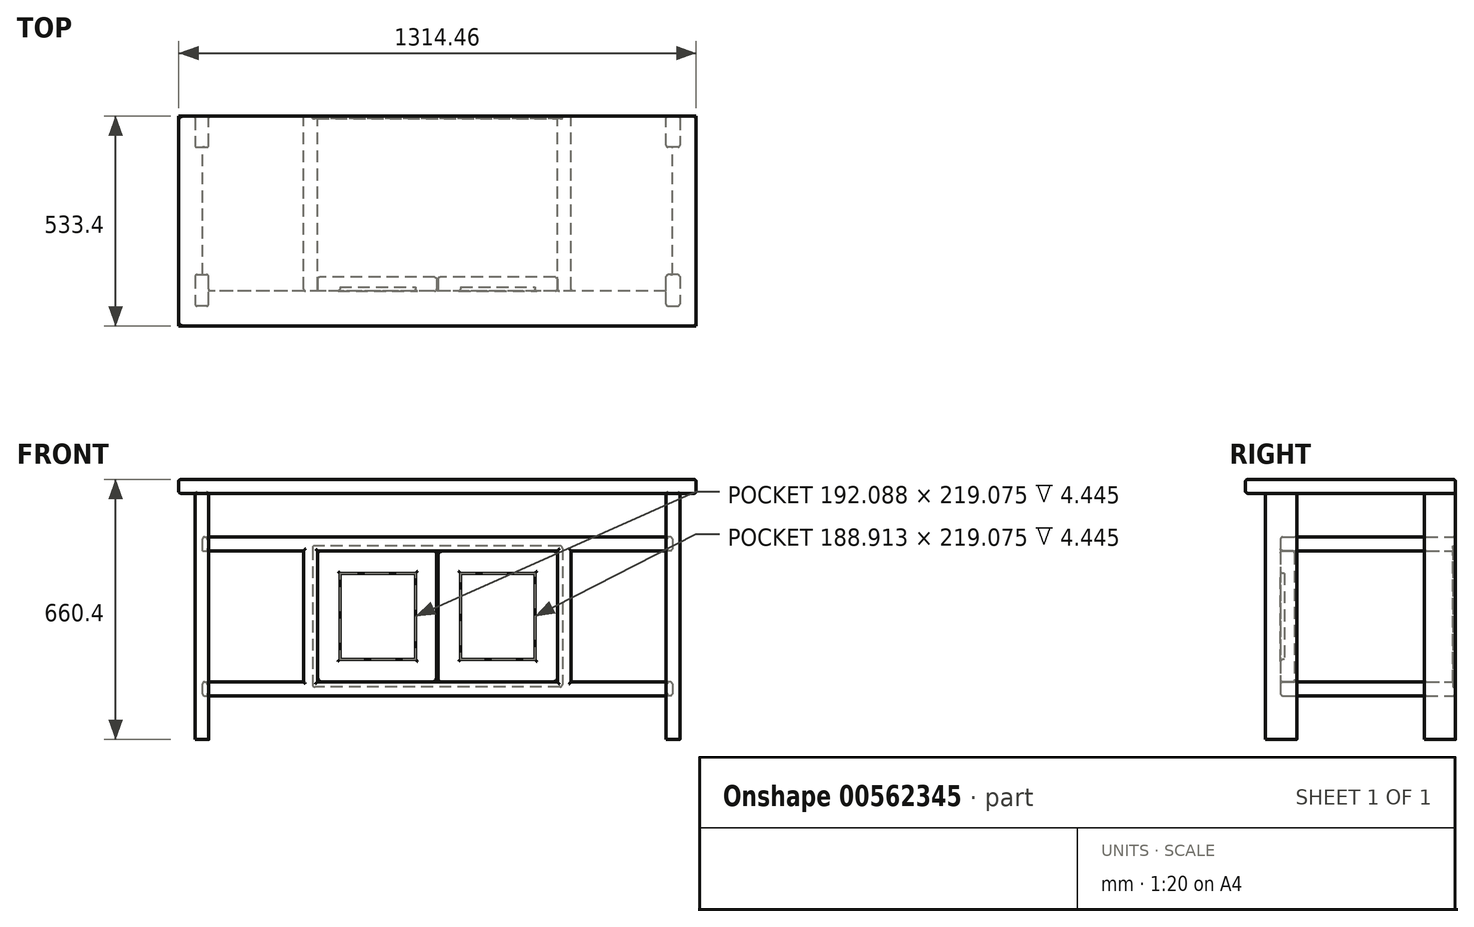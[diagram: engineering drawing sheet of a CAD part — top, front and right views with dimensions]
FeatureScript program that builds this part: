
annotation { "Feature Type Name" : "Feature", "Feature Type Description" : "" }
export const myFeature = defineFeature(function(context is Context, id is Id, definition is map)
    precondition{}
    {
        {
            var Q0;
            Q0=qCreatedBy(makeId("Front.planeOp"),FACE);
            var sketch = newSketch(context, id + "F0", { "sketchPlane" : qUnion([Q0])});
            skLineSegment(sketch, "E0.bottom", {"start": v(657.23, 660.4) * mm, "end": v(-657.23, 660.4) * mm});
            skLineSegment(sketch, "E0.top", {"start": v(657.22, 625.48) * mm, "end": v(-657.23, 625.48) * mm});
            skLineSegment(sketch, "E0.left", {"start": v(657.23, 660.4) * mm, "end": v(657.23, 625.48) * mm});
            skLineSegment(sketch, "E0.right", {"start": v(-657.23, 660.4) * mm, "end": v(-657.23, 625.48) * mm});
            skPoint(sketch, "E0.middle", {"position": v(0, 642.94) * mm});
            skLineSegment(sketch, "E1.bottom", {"start": v(596.9, 514.35) * mm, "end": v(-596.9, 514.35) * mm});
            skLineSegment(sketch, "E1.top", {"start": v(596.9, 479.43) * mm, "end": v(339.73, 479.43) * mm});
            skLineSegment(sketch, "E1.left", {"start": v(596.9, 514.35) * mm, "end": v(596.9, 479.43) * mm});
            skLineSegment(sketch, "E1.right", {"start": v(-596.9, 514.35) * mm, "end": v(-596.9, 479.43) * mm});
            skPoint(sketch, "E1.middle", {"position": v(0, 496.89) * mm});
            skLineSegment(sketch, "E2.bottom", {"start": v(596.9, 146.05) * mm, "end": v(339.73, 146.05) * mm});
            skLineSegment(sketch, "E2.top", {"start": v(596.9, 111.13) * mm, "end": v(-596.9, 111.13) * mm});
            skLineSegment(sketch, "E2.left", {"start": v(596.9, 146.05) * mm, "end": v(596.9, 111.13) * mm});
            skLineSegment(sketch, "E2.right", {"start": v(-596.9, 146.05) * mm, "end": v(-596.9, 111.13) * mm});
            skPoint(sketch, "E2.middle", {"position": v(0, 128.59) * mm});
            skLineSegment(sketch, "E3", {"start": v(304.8, 479.43) * mm, "end": v(304.8, 146.05) * mm});
            skLineSegment(sketch, "E4", {"start": v(339.73, 479.43) * mm, "end": v(339.73, 146.05) * mm});
            skLineSegment(sketch, "E5", {"start": v(0, 0) * mm, "end": v(0, -92.6) * mm, "construction": true});
            skLineSegment(sketch, "E6.MirrorCS", {"start": v(-304.8, 479.43) * mm, "end": v(-304.8, 146.05) * mm});
            skLineSegment(sketch, "E7.MirrorCS", {"start": v(-339.73, 479.43) * mm, "end": v(-339.73, 146.05) * mm});
            skLineSegment(sketch, "E8.trimOffspring", {"start": v(304.8, 479.43) * mm, "end": v(-304.8, 479.43) * mm});
            skLineSegment(sketch, "E9.trimOffspring", {"start": v(304.8, 146.05) * mm, "end": v(-304.8, 146.05) * mm});
            skLineSegment(sketch, "E10.trimOffspring", {"start": v(-339.73, 146.05) * mm, "end": v(-596.9, 146.05) * mm});
            skLineSegment(sketch, "E11.trimOffspring", {"start": v(-339.73, 479.43) * mm, "end": v(-596.9, 479.43) * mm});
            skLineSegment(sketch, "E12", {"start": v(304.8, 479.43) * mm, "end": v(339.73, 479.43) * mm, "construction": true});
            skSolve(sketch);
        }
        {
            var Q0;
            Q0=makeQuery(id+"F0.imprint","IMPRINT",FACE,{"disambiguationData":[TD([[makeQuery(id+"F0.imprint","IMPRINT",EDGE,{"derivedFrom":sQuery(id+"F0.wireOp",EDGE,"E1.bottom")}),1.0]])]});
            extrude(context, id + "F1", {"entities" : qUnion([Q0]), "depth" : 444.5 * mm, "offsetDistance" : 25.4 * mm});
        }
        {
            var Q0;
            Q0=makeQuery(id+"F0.imprint","IMPRINT",FACE,{"disambiguationData":[TD([[makeQuery(id+"F0.imprint","IMPRINT",EDGE,{"derivedFrom":sQuery(id+"F0.wireOp",EDGE,"E0.bottom")}),1.0]])]});
            extrude(context, id + "F2", {"entities" : qUnion([Q0]), "depth" : 533.4 * mm, "offsetDistance" : 25.4 * mm});
        }
        {
            var Q0;
            Q0=qCreatedBy(makeId("Top.planeOp"),FACE);
            var sketch = newSketch(context, id + "F3", { "sketchPlane" : qUnion([Q0])});
            skLineSegment(sketch, "E13.bottom", {"start": v(-615.95, -79.37) * mm, "end": v(-581.03, -79.37) * mm});
            skLineSegment(sketch, "E13.top", {"start": v(-615.95, 0) * mm, "end": v(-581.03, 0) * mm});
            skLineSegment(sketch, "E13.left", {"start": v(-615.95, -79.38) * mm, "end": v(-615.95, 0) * mm});
            skLineSegment(sketch, "E13.right", {"start": v(-581.03, -79.38) * mm, "end": v(-581.03, 0) * mm});
            skLineSegment(sketch, "E14.bottom", {"start": v(-615.95, -482.6) * mm, "end": v(-581.03, -482.6) * mm});
            skLineSegment(sketch, "E14.top", {"start": v(-615.95, -403.23) * mm, "end": v(-581.03, -403.23) * mm});
            skLineSegment(sketch, "E14.left", {"start": v(-615.95, -482.6) * mm, "end": v(-615.95, -403.23) * mm});
            skLineSegment(sketch, "E14.right", {"start": v(-581.03, -482.6) * mm, "end": v(-581.03, -403.23) * mm});
            skLineSegment(sketch, "E15", {"start": v(0, 0) * mm, "end": v(0, -190.92) * mm, "construction": true});
            skLineSegment(sketch, "E16.MirrorCS", {"start": v(615.95, -79.37) * mm, "end": v(581.03, -79.37) * mm});
            skLineSegment(sketch, "E17.MirrorCS", {"start": v(615.95, 0) * mm, "end": v(581.03, 0) * mm});
            skLineSegment(sketch, "E18.MirrorCS", {"start": v(615.95, -482.6) * mm, "end": v(581.03, -482.6) * mm});
            skLineSegment(sketch, "E19.MirrorCS", {"start": v(615.95, -403.23) * mm, "end": v(581.03, -403.23) * mm});
            skLineSegment(sketch, "E20.MirrorCS", {"start": v(581.03, -482.6) * mm, "end": v(581.03, -403.23) * mm});
            skLineSegment(sketch, "E21.MirrorCS", {"start": v(615.95, -79.38) * mm, "end": v(615.95, 0) * mm});
            skLineSegment(sketch, "E22.MirrorCS", {"start": v(615.95, -482.6) * mm, "end": v(615.95, -403.23) * mm});
            skLineSegment(sketch, "E23.MirrorCS", {"start": v(581.03, -79.38) * mm, "end": v(581.03, 0) * mm});
            skSolve(sketch);
        }
        {
            var Q0;
            Q0 = qSketchRegion(id + "F3", true);
            var Q1;
            Q1=makeQuery(id+"F2.opExtrude","SWEPT_FACE",FACE,{"disambiguationData":[OSD([sQuery(id+"F0.wireOp",EDGE,"E0.top")])]});
            extrude(context, id + "F4", {"entities" : qUnion([Q0]), "operationType" : NewBodyOperationType.ADD, "endBound" : BoundingType.UP_TO_SURFACE, "depth" : 25.4 * mm, "endBoundEntityFace" : qUnion([Q1]), "offsetDistance" : 25.4 * mm});
        }
        {
            var Q0;
            Q0=makeQuery(id+"F4.boolean.opBoolean","MERGE",FACE,{"derivedFrom":[makeQuery(id+"F1.opExtrude","CAP_FACE",FACE,{"disambiguationData":[OSD([sQuery(id+"F0.wireOp",EDGE,"E1.bottom"),sQuery(id+"F0.wireOp",EDGE,"E1.top"),sQuery(id+"F0.wireOp",EDGE,"E1.left"),sQuery(id+"F0.wireOp",EDGE,"E1.right"),sQuery(id+"F0.wireOp",EDGE,"E2.bottom"),sQuery(id+"F0.wireOp",EDGE,"E2.top"),sQuery(id+"F0.wireOp",EDGE,"E2.left"),sQuery(id+"F0.wireOp",EDGE,"E2.right"),sQuery(id+"F0.wireOp",EDGE,"E3"),sQuery(id+"F0.wireOp",EDGE,"E4"),sQuery(id+"F0.wireOp",EDGE,"E6.MirrorCS"),sQuery(id+"F0.wireOp",EDGE,"E7.MirrorCS"),sQuery(id+"F0.wireOp",EDGE,"E8.trimOffspring"),sQuery(id+"F0.wireOp",EDGE,"E9.trimOffspring"),sQuery(id+"F0.wireOp",EDGE,"E10.trimOffspring"),sQuery(id+"F0.wireOp",EDGE,"E11.trimOffspring")])],"isStart":true}),makeQuery(id+"F2.opExtrude","CAP_FACE",FACE,{"disambiguationData":[OSD([sQuery(id+"F0.wireOp",EDGE,"E0.bottom"),sQuery(id+"F0.wireOp",EDGE,"E0.top"),sQuery(id+"F0.wireOp",EDGE,"E0.left"),sQuery(id+"F0.wireOp",EDGE,"E0.right")])],"isStart":true}),makeQuery(id+"F4.opExtrude","SWEPT_FACE",FACE,{"disambiguationData":[OSD([sQuery(id+"F3.wireOp",EDGE,"E13.top")])]}),makeQuery(id+"F4.opExtrude","SWEPT_FACE",FACE,{"disambiguationData":[OSD([sQuery(id+"F3.wireOp",EDGE,"E17.MirrorCS")])]})]});
            var sketch = newSketch(context, id + "F5", { "sketchPlane" : qUnion([Q0])});
            skLineSegment(sketch, "E24.0", {"start": v(-311.15, 492.13) * mm, "end": v(311.15, 492.13) * mm});
            skLineSegment(sketch, "E24.1", {"start": v(-317.5, 485.78) * mm, "end": v(-317.5, 139.7) * mm});
            skLineSegment(sketch, "E24.2", {"start": v(-311.15, 133.35) * mm, "end": v(311.15, 133.35) * mm});
            skLineSegment(sketch, "E24.3", {"start": v(317.5, 485.78) * mm, "end": v(317.5, 139.7) * mm});
            skPoint(sketch, "E25.visualSharp", {"position": v(-317.5, 492.13) * mm});
            skArc(sketch, "E25.filletArc", {"start": v(-311.15, 492.13) * mm, "mid": v(-315.64, 490.27) * mm, "end": v(-317.5, 485.78) * mm});
            skPoint(sketch, "E26.visualSharp", {"position": v(317.5, 492.13) * mm});
            skArc(sketch, "E26.filletArc", {"start": v(317.5, 485.78) * mm, "mid": v(315.64, 490.27) * mm, "end": v(311.15, 492.13) * mm});
            skPoint(sketch, "E27.visualSharp", {"position": v(317.5, 133.35) * mm});
            skArc(sketch, "E27.filletArc", {"start": v(311.15, 133.35) * mm, "mid": v(315.64, 135.2) * mm, "end": v(317.5, 139.7) * mm});
            skPoint(sketch, "E28.visualSharp", {"position": v(-317.5, 133.35) * mm});
            skArc(sketch, "E28.filletArc", {"start": v(-317.5, 139.7) * mm, "mid": v(-315.64, 135.2) * mm, "end": v(-311.15, 133.35) * mm});
            skSolve(sketch);
        }
        {
            var Q0;
            Q0 = qSketchRegion(id + "F5", true);
            extrude(context, id + "F6", {"entities" : qUnion([Q0]), "oppositeDirection" : true, "depth" : 6.35 * mm, "offsetDistance" : 25.4 * mm});
        }
        {
            var Q0;
            Q0=makeQuery(id+"F6.opExtrude","SWEPT_BODY",BODY,{"disambiguationData":[OSD([sQuery(id+"F5.wireOp",EDGE,"E24.0"),sQuery(id+"F5.wireOp",EDGE,"E24.1"),sQuery(id+"F5.wireOp",EDGE,"E24.2"),sQuery(id+"F5.wireOp",EDGE,"E24.3"),sQuery(id+"F5.wireOp",EDGE,"E25.filletArc"),sQuery(id+"F5.wireOp",EDGE,"E26.filletArc"),sQuery(id+"F5.wireOp",EDGE,"E27.filletArc"),sQuery(id+"F5.wireOp",EDGE,"E28.filletArc")])]});
            var Q1;
            Q1=makeQuery(id+"F1.opExtrude","SWEPT_BODY",BODY,{"disambiguationData":[OSD([sQuery(id+"F0.wireOp",EDGE,"E1.bottom"),sQuery(id+"F0.wireOp",EDGE,"E1.top"),sQuery(id+"F0.wireOp",EDGE,"E1.left"),sQuery(id+"F0.wireOp",EDGE,"E1.right"),sQuery(id+"F0.wireOp",EDGE,"E2.bottom"),sQuery(id+"F0.wireOp",EDGE,"E2.top"),sQuery(id+"F0.wireOp",EDGE,"E2.left"),sQuery(id+"F0.wireOp",EDGE,"E2.right"),sQuery(id+"F0.wireOp",EDGE,"E3"),sQuery(id+"F0.wireOp",EDGE,"E4"),sQuery(id+"F0.wireOp",EDGE,"E6.MirrorCS"),sQuery(id+"F0.wireOp",EDGE,"E7.MirrorCS"),sQuery(id+"F0.wireOp",EDGE,"E8.trimOffspring"),sQuery(id+"F0.wireOp",EDGE,"E9.trimOffspring"),sQuery(id+"F0.wireOp",EDGE,"E10.trimOffspring"),sQuery(id+"F0.wireOp",EDGE,"E11.trimOffspring")])]});
            booleanBodies(context, id + "F7", {"operationType" : BooleanOperationType.SUBTRACTION, "tools" : qUnion([Q0]), "targets" : qUnion([Q1]), "keepTools" : true});
        }
        {
            var Q0;
            Q0=makeQuery(id+"F1.opExtrude","CAP_FACE",FACE,{"disambiguationData":[OSD([sQuery(id+"F0.wireOp",EDGE,"E1.bottom"),sQuery(id+"F0.wireOp",EDGE,"E1.top"),sQuery(id+"F0.wireOp",EDGE,"E1.left"),sQuery(id+"F0.wireOp",EDGE,"E1.right"),sQuery(id+"F0.wireOp",EDGE,"E2.bottom"),sQuery(id+"F0.wireOp",EDGE,"E2.top"),sQuery(id+"F0.wireOp",EDGE,"E2.left"),sQuery(id+"F0.wireOp",EDGE,"E2.right"),sQuery(id+"F0.wireOp",EDGE,"E3"),sQuery(id+"F0.wireOp",EDGE,"E4"),sQuery(id+"F0.wireOp",EDGE,"E6.MirrorCS"),sQuery(id+"F0.wireOp",EDGE,"E7.MirrorCS"),sQuery(id+"F0.wireOp",EDGE,"E8.trimOffspring"),sQuery(id+"F0.wireOp",EDGE,"E9.trimOffspring"),sQuery(id+"F0.wireOp",EDGE,"E10.trimOffspring"),sQuery(id+"F0.wireOp",EDGE,"E11.trimOffspring")])],"isStart":false});
            var sketch = newSketch(context, id + "F8", { "sketchPlane" : qUnion([Q0])});
            skLineSegment(sketch, "E29.bottom", {"start": v(-304.8, 479.43) * mm, "end": v(-1.59, 479.43) * mm});
            skLineSegment(sketch, "E29.top", {"start": v(-304.8, 146.05) * mm, "end": v(-1.59, 146.05) * mm});
            skLineSegment(sketch, "E29.left", {"start": v(-304.8, 479.43) * mm, "end": v(-304.8, 146.05) * mm});
            skLineSegment(sketch, "E29.right", {"start": v(-1.59, 479.43) * mm, "end": v(-1.59, 146.05) * mm});
            skLineSegment(sketch, "E30.bottom", {"start": v(1.59, 146.05) * mm, "end": v(304.8, 146.05) * mm});
            skLineSegment(sketch, "E30.top", {"start": v(1.59, 479.43) * mm, "end": v(304.8, 479.43) * mm});
            skLineSegment(sketch, "E30.left", {"start": v(1.59, 146.05) * mm, "end": v(1.59, 479.43) * mm});
            skLineSegment(sketch, "E30.right", {"start": v(304.8, 146.05) * mm, "end": v(304.8, 479.43) * mm});
            skLineSegment(sketch, "E31.0", {"start": v(-247.65, 422.28) * mm, "end": v(-55.56, 422.28) * mm});
            skLineSegment(sketch, "E31.1", {"start": v(-247.65, 422.28) * mm, "end": v(-247.65, 203.2) * mm});
            skLineSegment(sketch, "E31.2", {"start": v(-247.65, 203.2) * mm, "end": v(-55.56, 203.2) * mm});
            skLineSegment(sketch, "E31.3", {"start": v(-55.56, 203.2) * mm, "end": v(-55.56, 422.28) * mm});
            skLineSegment(sketch, "E32.0", {"start": v(58.74, 422.28) * mm, "end": v(247.65, 422.28) * mm});
            skLineSegment(sketch, "E32.1", {"start": v(58.74, 203.2) * mm, "end": v(58.74, 422.28) * mm});
            skLineSegment(sketch, "E32.2", {"start": v(58.74, 203.2) * mm, "end": v(247.65, 203.2) * mm});
            skLineSegment(sketch, "E32.3", {"start": v(247.65, 203.2) * mm, "end": v(247.65, 422.28) * mm});
            skPoint(sketch, "E33", {"position": v(0, 111.13) * mm});
            skSolve(sketch);
        }
        {
            var Q0;
            Q0 = qSketchRegion(id + "F8", true);
            var Q1;
            Q1=makeQuery(id+"F8.imprint","IMPRINT",FACE,{"disambiguationData":[TD([[makeQuery(id+"F8.imprint","IMPRINT",EDGE,{"derivedFrom":sQuery(id+"F8.wireOp",EDGE,"E31.0")}),-1.0]])]});
            var Q2;
            Q2=makeQuery(id+"F8.imprint","IMPRINT",FACE,{"disambiguationData":[TD([[makeQuery(id+"F8.imprint","IMPRINT",EDGE,{"derivedFrom":sQuery(id+"F8.wireOp",EDGE,"E32.0")}),-1.0]])]});
            extrude(context, id + "F9", {"entities" : qUnion([Q0, Q1, Q2]), "oppositeDirection" : true, "depth" : 34.92 * mm, "offsetDistance" : 25.4 * mm});
        }
        {
            var Q0;
            Q0=makeQuery(id+"F8.imprint","IMPRINT",FACE,{"disambiguationData":[TD([[makeQuery(id+"F8.imprint","IMPRINT",EDGE,{"derivedFrom":sQuery(id+"F8.wireOp",EDGE,"E31.0")}),-1.0]])]});
            var Q1;
            Q1=makeQuery(id+"F8.imprint","IMPRINT",FACE,{"disambiguationData":[TD([[makeQuery(id+"F8.imprint","IMPRINT",EDGE,{"derivedFrom":sQuery(id+"F8.wireOp",EDGE,"E32.0")}),-1.0]])]});
            extrude(context, id + "F10", {"entities" : qUnion([Q0, Q1]), "operationType" : NewBodyOperationType.REMOVE, "oppositeDirection" : true, "depth" : 9.52 * mm, "offsetDistance" : 25.4 * mm});
        }
        {
            var Q0;
            Q0=makeQuery(id+"F2.opExtrude","SWEPT_FACE",FACE,{"disambiguationData":[OSD([sQuery(id+"F0.wireOp",EDGE,"E0.bottom")])]});
            var Q1;
            Q1=makeQuery(id+"F2.opExtrude","CAP_EDGE",EDGE,{"disambiguationData":[OSD([sQuery(id+"F0.wireOp",EDGE,"E0.top")])],"isStart":false});
            var Q2;
            Q2=makeQuery(id+"F2.opExtrude","SWEPT_EDGE",EDGE,{"disambiguationData":[OSD([sQuery(id+"F0.wireOp",EDGE,"E0.top"),sQuery(id+"F0.wireOp",EDGE,"E0.right")])]});
            var Q3;
            Q3=makeQuery(id+"F2.opExtrude","SWEPT_EDGE",EDGE,{"disambiguationData":[OSD([sQuery(id+"F0.wireOp",EDGE,"E0.top"),sQuery(id+"F0.wireOp",EDGE,"E0.left")])]});
            var Q4;
            Q4=makeQuery(id+"F1.opExtrude","CAP_EDGE",EDGE,{"disambiguationData":[OSD([sQuery(id+"F0.wireOp",EDGE,"E1.bottom")])],"isStart":false});
            var Q5;
            Q5=makeQuery(id+"F1.opExtrude","CAP_EDGE",EDGE,{"disambiguationData":[OSD([sQuery(id+"F0.wireOp",EDGE,"E1.top")])],"isStart":false});
            var Q6;
            Q6=makeQuery(id+"F1.opExtrude","SWEPT_EDGE",EDGE,{"disambiguationData":[OSD([sQuery(id+"F0.wireOp",EDGE,"E1.bottom"),sQuery(id+"F0.wireOp",EDGE,"E1.left")])]});
            var Q7;
            Q7=makeQuery(id+"F1.opExtrude","SWEPT_EDGE",EDGE,{"disambiguationData":[OSD([sQuery(id+"F0.wireOp",EDGE,"E1.top"),sQuery(id+"F0.wireOp",EDGE,"E1.left")])]});
            var Q8;
            Q8=makeQuery(id+"F1.opExtrude","CAP_EDGE",EDGE,{"disambiguationData":[OSD([sQuery(id+"F0.wireOp",EDGE,"E1.bottom")])],"isStart":true});
            var Q9;
            Q9=makeQuery(id+"F1.opExtrude","CAP_EDGE",EDGE,{"disambiguationData":[OSD([sQuery(id+"F0.wireOp",EDGE,"E1.top")])],"isStart":true});
            var Q10;
            Q10=makeQuery(id+"F1.opExtrude","CAP_EDGE",EDGE,{"disambiguationData":[OSD([sQuery(id+"F0.wireOp",EDGE,"E11.trimOffspring")])],"isStart":true});
            var Q11;
            Q11=makeQuery(id+"F1.opExtrude","SWEPT_EDGE",EDGE,{"disambiguationData":[OSD([sQuery(id+"F0.wireOp",EDGE,"E1.bottom"),sQuery(id+"F0.wireOp",EDGE,"E1.right")])]});
            var Q12;
            Q12=makeQuery(id+"F4.opExtrude","SWEPT_EDGE",EDGE,{"disambiguationData":[OSD([sQuery(id+"F3.wireOp",EDGE,"E13.bottom"),sQuery(id+"F3.wireOp",EDGE,"E13.left")])]});
            var Q13;
            Q13=makeQuery(id+"F4.opExtrude","SWEPT_EDGE",EDGE,{"disambiguationData":[OSD([sQuery(id+"F3.wireOp",EDGE,"E13.top"),sQuery(id+"F3.wireOp",EDGE,"E13.left")])]});
            var Q14;
            Q14=makeQuery(id+"F4.opExtrude","SWEPT_EDGE",EDGE,{"disambiguationData":[OSD([sQuery(id+"F3.wireOp",EDGE,"E14.top"),sQuery(id+"F3.wireOp",EDGE,"E14.left")])]});
            var Q15;
            Q15=makeQuery(id+"F4.opExtrude","SWEPT_EDGE",EDGE,{"disambiguationData":[OSD([sQuery(id+"F3.wireOp",EDGE,"E14.bottom"),sQuery(id+"F3.wireOp",EDGE,"E14.right")])]});
            var Q16;
            Q16=makeQuery(id+"F4.opExtrude","SWEPT_EDGE",EDGE,{"disambiguationData":[OSD([sQuery(id+"F3.wireOp",EDGE,"E14.bottom"),sQuery(id+"F3.wireOp",EDGE,"E14.left")])]});
            var Q17;
            Q17=makeQuery(id+"F4.opExtrude","SWEPT_EDGE",EDGE,{"disambiguationData":[OSD([sQuery(id+"F3.wireOp",EDGE,"E18.MirrorCS"),sQuery(id+"F3.wireOp",EDGE,"E20.MirrorCS")])]});
            var Q18;
            Q18=makeQuery(id+"F4.opExtrude","SWEPT_EDGE",EDGE,{"disambiguationData":[OSD([sQuery(id+"F3.wireOp",EDGE,"E18.MirrorCS"),sQuery(id+"F3.wireOp",EDGE,"E22.MirrorCS")])]});
            var Q19;
            Q19=makeQuery(id+"F4.opExtrude","SWEPT_EDGE",EDGE,{"disambiguationData":[OSD([sQuery(id+"F3.wireOp",EDGE,"E19.MirrorCS"),sQuery(id+"F3.wireOp",EDGE,"E22.MirrorCS")])]});
            var Q20;
            Q20=makeQuery(id+"F4.opExtrude","SWEPT_EDGE",EDGE,{"disambiguationData":[OSD([sQuery(id+"F3.wireOp",EDGE,"E16.MirrorCS"),sQuery(id+"F3.wireOp",EDGE,"E21.MirrorCS")])]});
            var Q21;
            Q21=makeQuery(id+"F4.opExtrude","SWEPT_EDGE",EDGE,{"disambiguationData":[OSD([sQuery(id+"F3.wireOp",EDGE,"E17.MirrorCS"),sQuery(id+"F3.wireOp",EDGE,"E21.MirrorCS")])]});
            var Q22;
            {var subQ0=sQuery(id+"F0.wireOp",EDGE,"E1.top");var subQ2=sQuery(id+"F3.wireOp",EDGE,"E17.MirrorCS");var subQ3=sQuery(id+"F3.wireOp",EDGE,"E23.MirrorCS");Q22=makeQuery(id+"F4.boolean.opBoolean","SPLIT",EDGE,{"disambiguationData":[TD([makeQuery(id+"F1.opExtrude","SWEPT_FACE",FACE,{"disambiguationData":[OSD([subQ0])]})])],"derivedFrom":makeQuery(id+"F4.opExtrude","SWEPT_EDGE",EDGE,{"disambiguationData":[OSD([subQ2,subQ3])]})});}
            var Q23;
            Q23=makeQuery(id+"F1.opExtrude","CAP_EDGE",EDGE,{"disambiguationData":[OSD([sQuery(id+"F0.wireOp",EDGE,"E2.bottom")])],"isStart":true});
            var Q24;
            Q24=makeQuery(id+"F1.opExtrude","CAP_EDGE",EDGE,{"disambiguationData":[OSD([sQuery(id+"F0.wireOp",EDGE,"E2.top")])],"isStart":true});
            var Q25;
            Q25=makeQuery(id+"F1.opExtrude","CAP_EDGE",EDGE,{"disambiguationData":[OSD([sQuery(id+"F0.wireOp",EDGE,"E4")])],"isStart":true});
            var Q26;
            {var subQ0=sQuery(id+"F3.wireOp",EDGE,"E16.MirrorCS");var subQ1=sQuery(id+"F3.wireOp",EDGE,"E23.MirrorCS");Q26=makeQuery(id+"F4.boolean.opBoolean","SPLIT",EDGE,{"disambiguationData":[TD([makeQuery(id+"F1.opExtrude","SWEPT_FACE",FACE,{"disambiguationData":[OSD([sQuery(id+"F0.wireOp",EDGE,"E1.bottom")])]})])],"derivedFrom":makeQuery(id+"F4.opExtrude","SWEPT_EDGE",EDGE,{"disambiguationData":[OSD([subQ0,subQ1])]})});}
            var Q27;
            {var subQ0=sQuery(id+"F3.wireOp",EDGE,"E23.MirrorCS");var subQ1=sQuery(id+"F3.wireOp",EDGE,"E16.MirrorCS");Q27=makeQuery(id+"F4.boolean.opBoolean","SPLIT",EDGE,{"disambiguationData":[TD([makeQuery(id+"F1.opExtrude","SWEPT_FACE",FACE,{"disambiguationData":[OSD([sQuery(id+"F0.wireOp",EDGE,"E1.top")])]})])],"derivedFrom":makeQuery(id+"F4.opExtrude","SWEPT_EDGE",EDGE,{"disambiguationData":[OSD([subQ1,subQ0])]})});}
            var Q28;
            {var subQ0=sQuery(id+"F3.wireOp",EDGE,"E16.MirrorCS");var subQ1=sQuery(id+"F3.wireOp",EDGE,"E23.MirrorCS");Q28=makeQuery(id+"F4.boolean.opBoolean","SPLIT",EDGE,{"disambiguationData":[TD([makeQuery(id+"F1.opExtrude","SWEPT_FACE",FACE,{"disambiguationData":[OSD([sQuery(id+"F0.wireOp",EDGE,"E2.top")])]})])],"derivedFrom":makeQuery(id+"F4.opExtrude","SWEPT_EDGE",EDGE,{"disambiguationData":[OSD([subQ0,subQ1])]})});}
            var Q29;
            {var subQ0=sQuery(id+"F3.wireOp",EDGE,"E23.MirrorCS");var subQ1=sQuery(id+"F3.wireOp",EDGE,"E17.MirrorCS");var subQ2=sQuery(id+"F0.wireOp",EDGE,"E2.top");Q29=makeQuery(id+"F4.boolean.opBoolean","SPLIT",EDGE,{"disambiguationData":[TD([makeQuery(id+"F1.opExtrude","SWEPT_FACE",FACE,{"disambiguationData":[OSD([subQ2])]})])],"derivedFrom":makeQuery(id+"F4.opExtrude","SWEPT_EDGE",EDGE,{"disambiguationData":[OSD([subQ1,subQ0])]})});}
            var Q30;
            {var subQ1=sQuery(id+"F0.wireOp",EDGE,"E1.bottom");var subQ2=sQuery(id+"F3.wireOp",EDGE,"E17.MirrorCS");var subQ3=sQuery(id+"F3.wireOp",EDGE,"E23.MirrorCS");Q30=makeQuery(id+"F4.boolean.opBoolean","SPLIT",EDGE,{"disambiguationData":[TD([makeQuery(id+"F1.opExtrude","SWEPT_FACE",FACE,{"disambiguationData":[OSD([subQ1])]})])],"derivedFrom":makeQuery(id+"F4.opExtrude","SWEPT_EDGE",EDGE,{"disambiguationData":[OSD([subQ2,subQ3])]})});}
            var Q31;
            Q31=makeQuery(id+"F1.opExtrude","CAP_EDGE",EDGE,{"disambiguationData":[OSD([sQuery(id+"F0.wireOp",EDGE,"E10.trimOffspring")])],"isStart":true});
            var Q32;
            Q32=makeQuery(id+"F1.opExtrude","CAP_EDGE",EDGE,{"disambiguationData":[OSD([sQuery(id+"F0.wireOp",EDGE,"E7.MirrorCS")])],"isStart":true});
            var Q33;
            {var subQ0=sQuery(id+"F0.wireOp",EDGE,"E0.top");Q33=makeQuery(id+"F4.boolean.opBoolean","SPLIT",EDGE,{"disambiguationData":[TD([makeQuery(id+"F4.opExtrude","SWEPT_FACE",FACE,{"disambiguationData":[OSD([sQuery(id+"F3.wireOp",EDGE,"E13.right")])]})])],"derivedFrom":makeQuery(id+"F2.opExtrude","CAP_EDGE",EDGE,{"disambiguationData":[OSD([subQ0])],"isStart":true})});}
            var Q34;
            {var subQ0=sQuery(id+"F0.wireOp",EDGE,"E0.top");var subQ1=sQuery(id+"F0.wireOp",EDGE,"E0.right");Q34=makeQuery(id+"F4.boolean.opBoolean","SPLIT",EDGE,{"disambiguationData":[TD([makeQuery(id+"F2.opExtrude","SWEPT_FACE",FACE,{"disambiguationData":[OSD([subQ1])]})])],"derivedFrom":makeQuery(id+"F2.opExtrude","CAP_EDGE",EDGE,{"disambiguationData":[OSD([subQ0])],"isStart":true})});}
            var Q35;
            {var subQ0=sQuery(id+"F0.wireOp",EDGE,"E0.left");var subQ1=sQuery(id+"F0.wireOp",EDGE,"E0.top");Q35=makeQuery(id+"F4.boolean.opBoolean","SPLIT",EDGE,{"disambiguationData":[TD([makeQuery(id+"F2.opExtrude","SWEPT_FACE",FACE,{"disambiguationData":[OSD([subQ0])]})])],"derivedFrom":makeQuery(id+"F2.opExtrude","CAP_EDGE",EDGE,{"disambiguationData":[OSD([subQ1])],"isStart":true})});}
            var Q36;
            {var subQ0=sQuery(id+"F0.wireOp",EDGE,"E10.trimOffspring");var subQ2=sQuery(id+"F3.wireOp",EDGE,"E13.top");var subQ3=sQuery(id+"F3.wireOp",EDGE,"E13.right");Q36=makeQuery(id+"F4.boolean.opBoolean","SPLIT",EDGE,{"disambiguationData":[TD([makeQuery(id+"F1.opExtrude","SWEPT_FACE",FACE,{"disambiguationData":[OSD([subQ0])]})])],"derivedFrom":makeQuery(id+"F4.opExtrude","SWEPT_EDGE",EDGE,{"disambiguationData":[OSD([subQ2,subQ3])]})});}
            var Q37;
            {var subQ0=sQuery(id+"F3.wireOp",EDGE,"E13.bottom");var subQ1=sQuery(id+"F3.wireOp",EDGE,"E13.right");Q37=makeQuery(id+"F4.boolean.opBoolean","SPLIT",EDGE,{"disambiguationData":[TD([makeQuery(id+"F1.opExtrude","SWEPT_FACE",FACE,{"disambiguationData":[OSD([sQuery(id+"F0.wireOp",EDGE,"E10.trimOffspring")])]})])],"derivedFrom":makeQuery(id+"F4.opExtrude","SWEPT_EDGE",EDGE,{"disambiguationData":[OSD([subQ0,subQ1])]})});}
            var Q38;
            {var subQ0=sQuery(id+"F3.wireOp",EDGE,"E13.bottom");var subQ1=sQuery(id+"F3.wireOp",EDGE,"E13.right");Q38=makeQuery(id+"F4.boolean.opBoolean","SPLIT",EDGE,{"disambiguationData":[TD([makeQuery(id+"F1.opExtrude","SWEPT_FACE",FACE,{"disambiguationData":[OSD([sQuery(id+"F0.wireOp",EDGE,"E1.bottom")])]})])],"derivedFrom":makeQuery(id+"F4.opExtrude","SWEPT_EDGE",EDGE,{"disambiguationData":[OSD([subQ0,subQ1])]})});}
            var Q39;
            {var subQ1=sQuery(id+"F3.wireOp",EDGE,"E13.top");var subQ2=sQuery(id+"F0.wireOp",EDGE,"E1.bottom");var subQ3=sQuery(id+"F3.wireOp",EDGE,"E13.right");Q39=makeQuery(id+"F4.boolean.opBoolean","SPLIT",EDGE,{"disambiguationData":[TD([makeQuery(id+"F1.opExtrude","SWEPT_FACE",FACE,{"disambiguationData":[OSD([subQ2])]})])],"derivedFrom":makeQuery(id+"F4.opExtrude","SWEPT_EDGE",EDGE,{"disambiguationData":[OSD([subQ1,subQ3])]})});}
            var Q40;
            {var subQ0=sQuery(id+"F3.wireOp",EDGE,"E14.top");var subQ1=sQuery(id+"F3.wireOp",EDGE,"E14.right");Q40=makeQuery(id+"F4.boolean.opBoolean","SPLIT",EDGE,{"disambiguationData":[TD([makeQuery(id+"F1.opExtrude","SWEPT_FACE",FACE,{"disambiguationData":[OSD([sQuery(id+"F0.wireOp",EDGE,"E10.trimOffspring")])]})])],"derivedFrom":makeQuery(id+"F4.opExtrude","SWEPT_EDGE",EDGE,{"disambiguationData":[OSD([subQ0,subQ1])]})});}
            var Q41;
            {var subQ0=sQuery(id+"F3.wireOp",EDGE,"E14.top");var subQ1=sQuery(id+"F3.wireOp",EDGE,"E14.right");Q41=makeQuery(id+"F4.boolean.opBoolean","SPLIT",EDGE,{"disambiguationData":[TD([makeQuery(id+"F1.opExtrude","SWEPT_FACE",FACE,{"disambiguationData":[OSD([sQuery(id+"F0.wireOp",EDGE,"E1.bottom")])]})])],"derivedFrom":makeQuery(id+"F4.opExtrude","SWEPT_EDGE",EDGE,{"disambiguationData":[OSD([subQ0,subQ1])]})});}
            var Q42;
            {var subQ0=sQuery(id+"F3.wireOp",EDGE,"E14.right");var subQ1=sQuery(id+"F3.wireOp",EDGE,"E14.top");Q42=makeQuery(id+"F4.boolean.opBoolean","SPLIT",EDGE,{"disambiguationData":[TD([makeQuery(id+"F1.opExtrude","SWEPT_FACE",FACE,{"disambiguationData":[OSD([sQuery(id+"F0.wireOp",EDGE,"E2.top")])]})])],"derivedFrom":makeQuery(id+"F4.opExtrude","SWEPT_EDGE",EDGE,{"disambiguationData":[OSD([subQ1,subQ0])]})});}
            var Q43;
            {var subQ0=sQuery(id+"F3.wireOp",EDGE,"E13.right");var subQ1=sQuery(id+"F3.wireOp",EDGE,"E13.top");var subQ2=sQuery(id+"F0.wireOp",EDGE,"E2.top");Q43=makeQuery(id+"F4.boolean.opBoolean","SPLIT",EDGE,{"disambiguationData":[TD([makeQuery(id+"F1.opExtrude","SWEPT_FACE",FACE,{"disambiguationData":[OSD([subQ2])]})])],"derivedFrom":makeQuery(id+"F4.opExtrude","SWEPT_EDGE",EDGE,{"disambiguationData":[OSD([subQ1,subQ0])]})});}
            var Q44;
            {var subQ0=sQuery(id+"F3.wireOp",EDGE,"E13.bottom");var subQ1=sQuery(id+"F3.wireOp",EDGE,"E13.right");Q44=makeQuery(id+"F4.boolean.opBoolean","SPLIT",EDGE,{"disambiguationData":[TD([makeQuery(id+"F1.opExtrude","SWEPT_FACE",FACE,{"disambiguationData":[OSD([sQuery(id+"F0.wireOp",EDGE,"E2.top")])]})])],"derivedFrom":makeQuery(id+"F4.opExtrude","SWEPT_EDGE",EDGE,{"disambiguationData":[OSD([subQ0,subQ1])]})});}
            var Q45;
            {var subQ0=sQuery(id+"F3.wireOp",EDGE,"E20.MirrorCS");var subQ1=sQuery(id+"F3.wireOp",EDGE,"E19.MirrorCS");Q45=makeQuery(id+"F4.boolean.opBoolean","SPLIT",EDGE,{"disambiguationData":[TD([makeQuery(id+"F1.opExtrude","SWEPT_FACE",FACE,{"disambiguationData":[OSD([sQuery(id+"F0.wireOp",EDGE,"E1.bottom")])]})])],"derivedFrom":makeQuery(id+"F4.opExtrude","SWEPT_EDGE",EDGE,{"disambiguationData":[OSD([subQ1,subQ0])]})});}
            var Q46;
            {var subQ0=sQuery(id+"F3.wireOp",EDGE,"E19.MirrorCS");var subQ1=sQuery(id+"F3.wireOp",EDGE,"E20.MirrorCS");Q46=makeQuery(id+"F4.boolean.opBoolean","SPLIT",EDGE,{"disambiguationData":[TD([makeQuery(id+"F1.opExtrude","SWEPT_FACE",FACE,{"disambiguationData":[OSD([sQuery(id+"F0.wireOp",EDGE,"E1.top")])]})])],"derivedFrom":makeQuery(id+"F4.opExtrude","SWEPT_EDGE",EDGE,{"disambiguationData":[OSD([subQ0,subQ1])]})});}
            var Q47;
            {var subQ0=sQuery(id+"F3.wireOp",EDGE,"E20.MirrorCS");var subQ1=sQuery(id+"F3.wireOp",EDGE,"E19.MirrorCS");Q47=makeQuery(id+"F4.boolean.opBoolean","SPLIT",EDGE,{"disambiguationData":[TD([makeQuery(id+"F1.opExtrude","SWEPT_FACE",FACE,{"disambiguationData":[OSD([sQuery(id+"F0.wireOp",EDGE,"E2.top")])]})])],"derivedFrom":makeQuery(id+"F4.opExtrude","SWEPT_EDGE",EDGE,{"disambiguationData":[OSD([subQ1,subQ0])]})});}
            var Q48;
            Q48=makeQuery(id+"F1.opExtrude","CAP_EDGE",EDGE,{"disambiguationData":[OSD([sQuery(id+"F0.wireOp",EDGE,"E2.top")])],"isStart":false});
            var Q49;
            Q49=makeQuery(id+"F1.opExtrude","CAP_EDGE",EDGE,{"disambiguationData":[OSD([sQuery(id+"F0.wireOp",EDGE,"E2.bottom")])],"isStart":false});
            var Q50;
            Q50=makeQuery(id+"F1.opExtrude","CAP_EDGE",EDGE,{"disambiguationData":[OSD([sQuery(id+"F0.wireOp",EDGE,"E4")])],"isStart":false});
            var Q51;
            Q51=makeQuery(id+"F1.opExtrude","CAP_EDGE",EDGE,{"disambiguationData":[OSD([sQuery(id+"F0.wireOp",EDGE,"E7.MirrorCS")])],"isStart":false});
            var Q52;
            Q52=makeQuery(id+"F1.opExtrude","CAP_EDGE",EDGE,{"disambiguationData":[OSD([sQuery(id+"F0.wireOp",EDGE,"E11.trimOffspring")])],"isStart":false});
            var Q53;
            Q53=makeQuery(id+"F1.opExtrude","CAP_EDGE",EDGE,{"disambiguationData":[OSD([sQuery(id+"F0.wireOp",EDGE,"E10.trimOffspring")])],"isStart":false});
            var Q54;
            Q54=makeQuery(id+"F1.opExtrude","SWEPT_EDGE",EDGE,{"disambiguationData":[OSD([sQuery(id+"F0.wireOp",EDGE,"E2.bottom"),sQuery(id+"F0.wireOp",EDGE,"E2.left")])]});
            var Q55;
            Q55=makeQuery(id+"F1.opExtrude","SWEPT_EDGE",EDGE,{"disambiguationData":[OSD([sQuery(id+"F0.wireOp",EDGE,"E2.top"),sQuery(id+"F0.wireOp",EDGE,"E2.left")])]});
            var Q56;
            Q56=makeQuery(id+"F1.opExtrude","SWEPT_EDGE",EDGE,{"disambiguationData":[OSD([sQuery(id+"F0.wireOp",EDGE,"E2.right"),sQuery(id+"F0.wireOp",EDGE,"E10.trimOffspring")])]});
            var Q57;
            Q57=makeQuery(id+"F1.opExtrude","SWEPT_EDGE",EDGE,{"disambiguationData":[OSD([sQuery(id+"F0.wireOp",EDGE,"E2.top"),sQuery(id+"F0.wireOp",EDGE,"E2.right")])]});
            var Q58;
            Q58=makeQuery(id+"F1.opExtrude","CAP_EDGE",EDGE,{"disambiguationData":[OSD([sQuery(id+"F0.wireOp",EDGE,"E6.MirrorCS")])],"isStart":false});
            var Q59;
            Q59=makeQuery(id+"F1.opExtrude","CAP_EDGE",EDGE,{"disambiguationData":[OSD([sQuery(id+"F0.wireOp",EDGE,"E8.trimOffspring")])],"isStart":false});
            var Q60;
            Q60=makeQuery(id+"F1.opExtrude","CAP_EDGE",EDGE,{"disambiguationData":[OSD([sQuery(id+"F0.wireOp",EDGE,"E3")])],"isStart":false});
            var Q61;
            Q61=makeQuery(id+"F1.opExtrude","CAP_EDGE",EDGE,{"disambiguationData":[OSD([sQuery(id+"F0.wireOp",EDGE,"E9.trimOffspring")])],"isStart":false});
            fillet(context, id + "F11", {"entities" : qUnion([Q0, Q1, Q2, Q3, Q4, Q5, Q6, Q7, Q8, Q9, Q10, Q11, Q12, Q13, Q14, Q15, Q16, Q17, Q18, Q19, Q20, Q21, Q22, Q23, Q24, Q25, Q26, Q27, Q28, Q29, Q30, Q31, Q32, Q33, Q34, Q35, Q36, Q37, Q38, Q39, Q40, Q41, Q42, Q43, Q44, Q45, Q46, Q47, Q48, Q49, Q50, Q51, Q52, Q53, Q54, Q55, Q56, Q57, Q58, Q59, Q60, Q61]), "radius" : 5.08 * mm, "tangentPropagation" : true, "allowEdgeOverflow" : false});
        }
        {
            var Q0;
            Q0=makeQuery(id+"F9.opExtrude","CAP_FACE",FACE,{"disambiguationData":[OSD([sQuery(id+"F8.wireOp",EDGE,"E29.bottom"),sQuery(id+"F8.wireOp",EDGE,"E29.top"),sQuery(id+"F8.wireOp",EDGE,"E29.left"),sQuery(id+"F8.wireOp",EDGE,"E29.right")])],"isStart":true});
            var Q1;
            Q1=makeQuery(id+"F9.opExtrude","CAP_FACE",FACE,{"disambiguationData":[OSD([sQuery(id+"F8.wireOp",EDGE,"E30.bottom"),sQuery(id+"F8.wireOp",EDGE,"E30.top"),sQuery(id+"F8.wireOp",EDGE,"E30.left"),sQuery(id+"F8.wireOp",EDGE,"E30.right")])],"isStart":true});
            var Q2;
            Q2=makeQuery(id+"F9.opExtrude","CAP_FACE",FACE,{"disambiguationData":[OSD([sQuery(id+"F8.wireOp",EDGE,"E30.bottom"),sQuery(id+"F8.wireOp",EDGE,"E30.top"),sQuery(id+"F8.wireOp",EDGE,"E30.left"),sQuery(id+"F8.wireOp",EDGE,"E30.right")])],"isStart":false});
            var Q3;
            Q3=makeQuery(id+"F9.opExtrude","CAP_FACE",FACE,{"disambiguationData":[OSD([sQuery(id+"F8.wireOp",EDGE,"E29.bottom"),sQuery(id+"F8.wireOp",EDGE,"E29.top"),sQuery(id+"F8.wireOp",EDGE,"E29.left"),sQuery(id+"F8.wireOp",EDGE,"E29.right")])],"isStart":false});
            fillet(context, id + "F12", {"entities" : qUnion([Q0, Q1, Q2, Q3]), "radius" : 5.08 * mm, "tangentPropagation" : true, "allowEdgeOverflow" : false});
        }
    });
